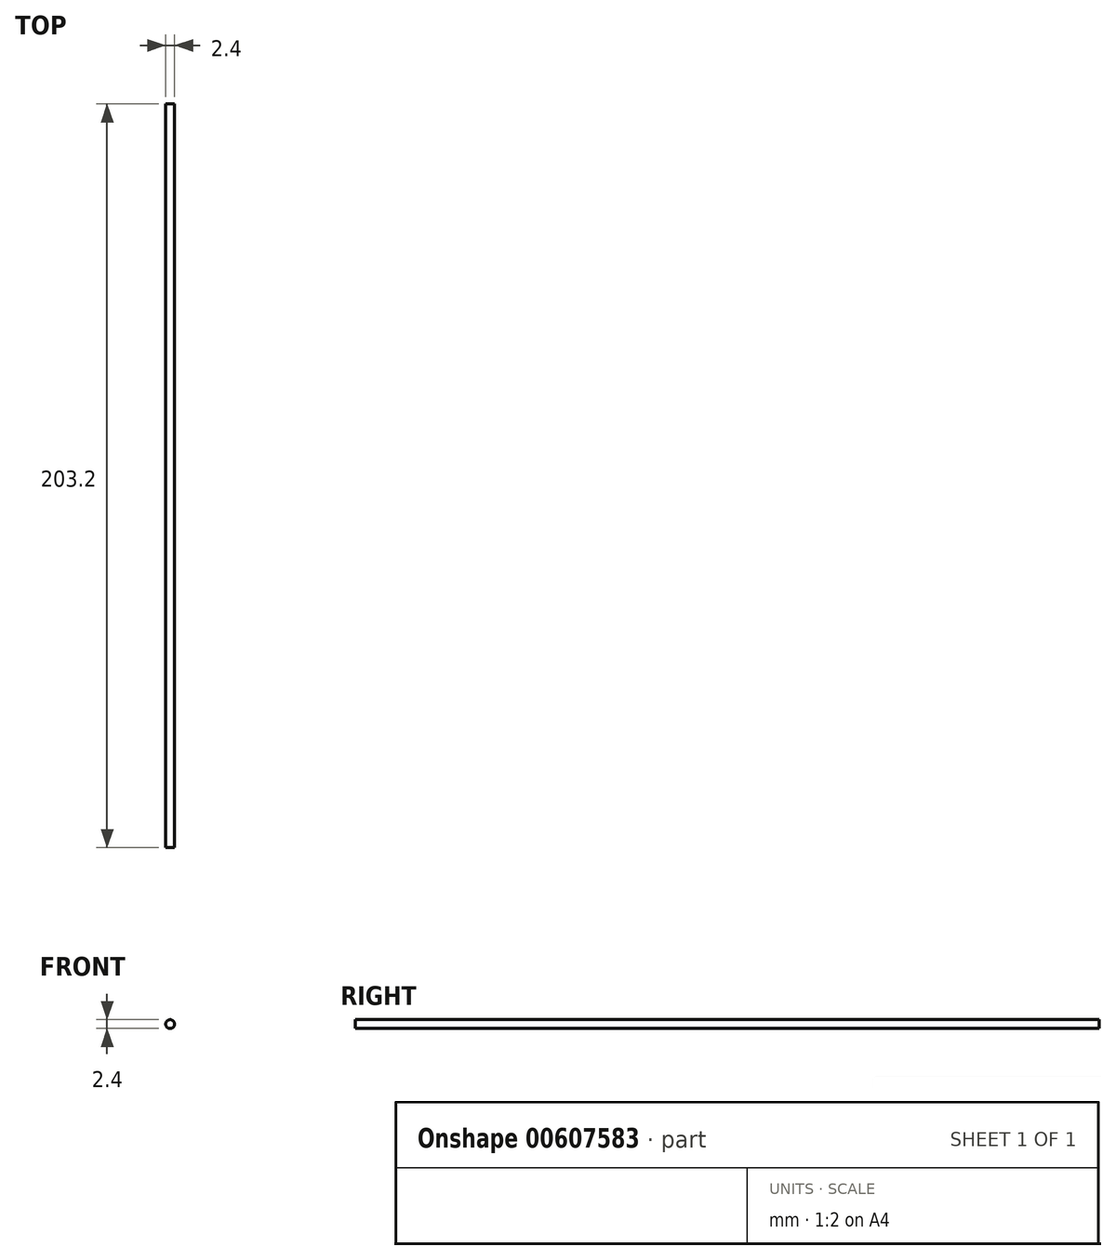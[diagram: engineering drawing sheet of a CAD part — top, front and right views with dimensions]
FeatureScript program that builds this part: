
annotation { "Feature Type Name" : "Feature", "Feature Type Description" : "" }
export const myFeature = defineFeature(function(context is Context, id is Id, definition is map)
    precondition{}
    {
        {
            var Q0;
            Q0=qCreatedBy(makeId("Front.planeOp"),FACE);
            var sketch = newSketch(context, id + "F0", { "sketchPlane" : qUnion([Q0])});
            skCircle(sketch, "E0", {"center": v(0, 0) * mm, "radius": 1.2 * mm});
            skSolve(sketch);
        }
        {
            var Q0;
            Q0 = qSketchRegion(id + "F0", true);
            extrude(context, id + "F1", {"entities" : qUnion([Q0]), "depth" : 203.2 * mm, "offsetDistance" : 25 * mm});
        }
    });
